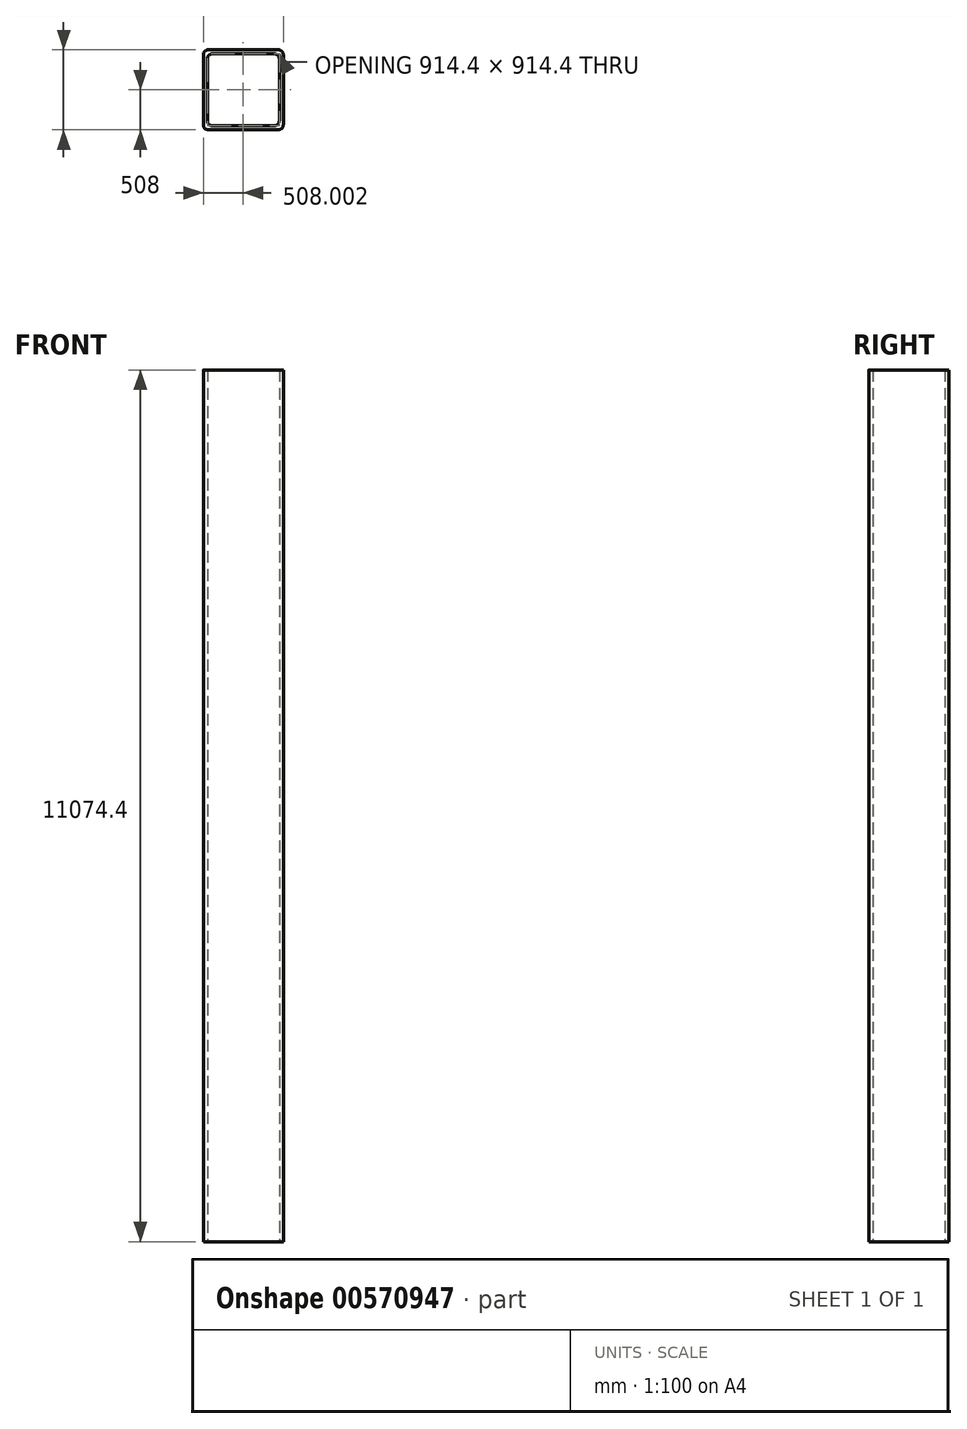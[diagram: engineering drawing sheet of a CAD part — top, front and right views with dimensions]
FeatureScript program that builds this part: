
annotation { "Feature Type Name" : "Feature", "Feature Type Description" : "" }
export const myFeature = defineFeature(function(context is Context, id is Id, definition is map)
    precondition{}
    {
        {
            var Q0;
            Q0=qCreatedBy(makeId("Top.planeOp"),FACE);
            var sketch = newSketch(context, id + "F0", { "sketchPlane" : qUnion([Q0])});
            skLineSegment(sketch, "E0.bottom", {"start": v(-441.17, 0) * mm, "end": v(447.83, 0) * mm});
            skLineSegment(sketch, "E0.top", {"start": v(-441.17, -1016) * mm, "end": v(447.83, -1016) * mm});
            skLineSegment(sketch, "E0.left", {"start": v(-504.67, -63.5) * mm, "end": v(-504.67, -952.5) * mm});
            skLineSegment(sketch, "E0.right", {"start": v(511.33, -63.5) * mm, "end": v(511.33, -952.5) * mm});
            skPoint(sketch, "E1.visualSharp", {"position": v(-504.67, 0) * mm});
            skArc(sketch, "E1.filletArc", {"start": v(-441.17, 0) * mm, "mid": v(-486.07, -18.6) * mm, "end": v(-504.67, -63.5) * mm});
            skPoint(sketch, "E2.visualSharp", {"position": v(511.33, 0) * mm});
            skArc(sketch, "E2.filletArc", {"start": v(511.33, -63.5) * mm, "mid": v(492.73, -18.6) * mm, "end": v(447.83, 0) * mm});
            skPoint(sketch, "E3.visualSharp", {"position": v(511.33, -1016) * mm});
            skArc(sketch, "E3.filletArc", {"start": v(447.83, -1016) * mm, "mid": v(492.73, -997.4) * mm, "end": v(511.33, -952.5) * mm});
            skPoint(sketch, "E4.visualSharp", {"position": v(-504.67, -1016) * mm});
            skArc(sketch, "E4.filletArc", {"start": v(-504.67, -952.5) * mm, "mid": v(-486.07, -997.4) * mm, "end": v(-441.17, -1016) * mm});
            skLineSegment(sketch, "E5.bottom", {"start": v(-390.37, -50.8) * mm, "end": v(397.03, -50.8) * mm});
            skLineSegment(sketch, "E5.top", {"start": v(-390.37, -965.2) * mm, "end": v(397.03, -965.2) * mm});
            skLineSegment(sketch, "E5.left", {"start": v(-453.87, -114.3) * mm, "end": v(-453.87, -901.7) * mm});
            skLineSegment(sketch, "E5.right", {"start": v(460.53, -114.3) * mm, "end": v(460.53, -901.7) * mm});
            skPoint(sketch, "E6.visualSharp", {"position": v(-453.87, -50.8) * mm});
            skArc(sketch, "E6.filletArc", {"start": v(-390.37, -50.8) * mm, "mid": v(-435.27, -69.4) * mm, "end": v(-453.87, -114.3) * mm});
            skPoint(sketch, "E7.visualSharp", {"position": v(460.53, -50.8) * mm});
            skArc(sketch, "E7.filletArc", {"start": v(460.53, -114.3) * mm, "mid": v(441.93, -69.4) * mm, "end": v(397.03, -50.8) * mm});
            skPoint(sketch, "E8.visualSharp", {"position": v(460.53, -965.2) * mm});
            skArc(sketch, "E8.filletArc", {"start": v(397.03, -965.2) * mm, "mid": v(441.93, -946.6) * mm, "end": v(460.53, -901.7) * mm});
            skPoint(sketch, "E9.visualSharp", {"position": v(-453.87, -965.2) * mm});
            skArc(sketch, "E9.filletArc", {"start": v(-453.87, -901.7) * mm, "mid": v(-435.27, -946.6) * mm, "end": v(-390.37, -965.2) * mm});
            skSolve(sketch);
        }
        {
            var Q0;
            Q0 = qSketchRegion(id + "F0", true);
            extrude(context, id + "F1", {"entities" : qUnion([Q0]), "depth" : 11074.4 * mm, "offsetDistance" : 25.4 * mm});
        }
    });
